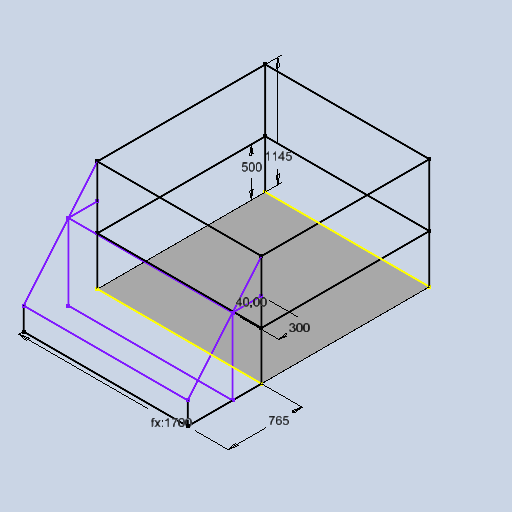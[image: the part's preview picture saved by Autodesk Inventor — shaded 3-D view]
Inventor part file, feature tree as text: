
AUTODESK INVENTOR PART (.ipt)
format: ipt  version: 2025 (Build 290162010, 162A)  size: 120,832 bytes
history: native  units: mm
features: sketch x2, extrude x1
ambient origin geometry x8: Origin, YZ Plane, XZ Plane, XY Plane, X Axis, Y Axis, Z Axis, Center Point
bodies: Solid1 (feature_tree)
feature tree (3):
  extrude  "Extrusion1"  Depth=1740.0mm
  sketch  "3D Sketch1"
  sketch  "Sketch1"  dims[d0=1700.0mm d1=1740.0mm d2=1.0mm d3=0.0mm d4=1145.0mm d7=500.0mm d8=1700.0mm d14=765.000058mm d15=300.0mm d16=6.981317mm]
